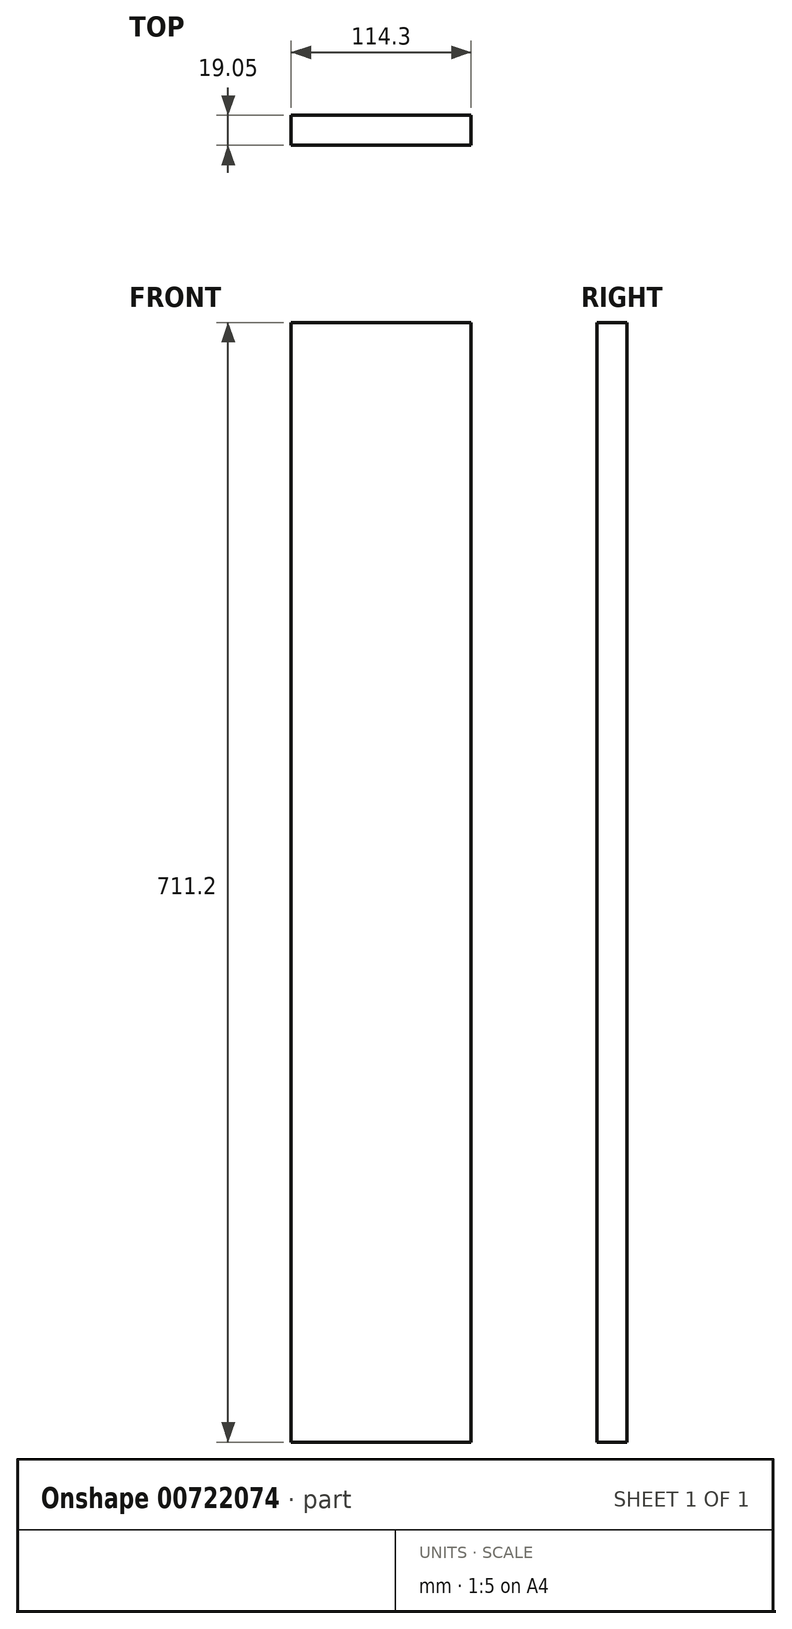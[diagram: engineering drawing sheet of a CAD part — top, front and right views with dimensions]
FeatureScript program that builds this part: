
annotation { "Feature Type Name" : "Feature", "Feature Type Description" : "" }
export const myFeature = defineFeature(function(context is Context, id is Id, definition is map)
    precondition{}
    {
        {
            var Q0;
            Q0=qCreatedBy(makeId("Front.planeOp"),FACE);
            var sketch = newSketch(context, id + "F0", { "sketchPlane" : qUnion([Q0])});
            skLineSegment(sketch, "E0.bottom", {"start": v(57.15, 355.6) * mm, "end": v(-57.15, 355.6) * mm});
            skLineSegment(sketch, "E0.top", {"start": v(57.15, -355.6) * mm, "end": v(-57.15, -355.6) * mm});
            skLineSegment(sketch, "E0.left", {"start": v(57.15, 355.6) * mm, "end": v(57.15, -355.6) * mm});
            skLineSegment(sketch, "E0.right", {"start": v(-57.15, 355.6) * mm, "end": v(-57.15, -355.6) * mm});
            skPoint(sketch, "E0.middle", {"position": v(0, 0) * mm});
            skSolve(sketch);
        }
        {
            var Q0;
            Q0=makeQuery(id+"F0.imprint","IMPRINT",FACE,{"disambiguationData":[TD([[makeQuery(id+"F0.imprint","IMPRINT",EDGE,{"derivedFrom":sQuery(id+"F0.wireOp",EDGE,"E0.bottom")}),1.0]])]});
            extrude(context, id + "F1", {"entities" : qUnion([Q0]), "depth" : 19.05 * mm, "offsetDistance" : 25.4 * mm});
        }
    });
